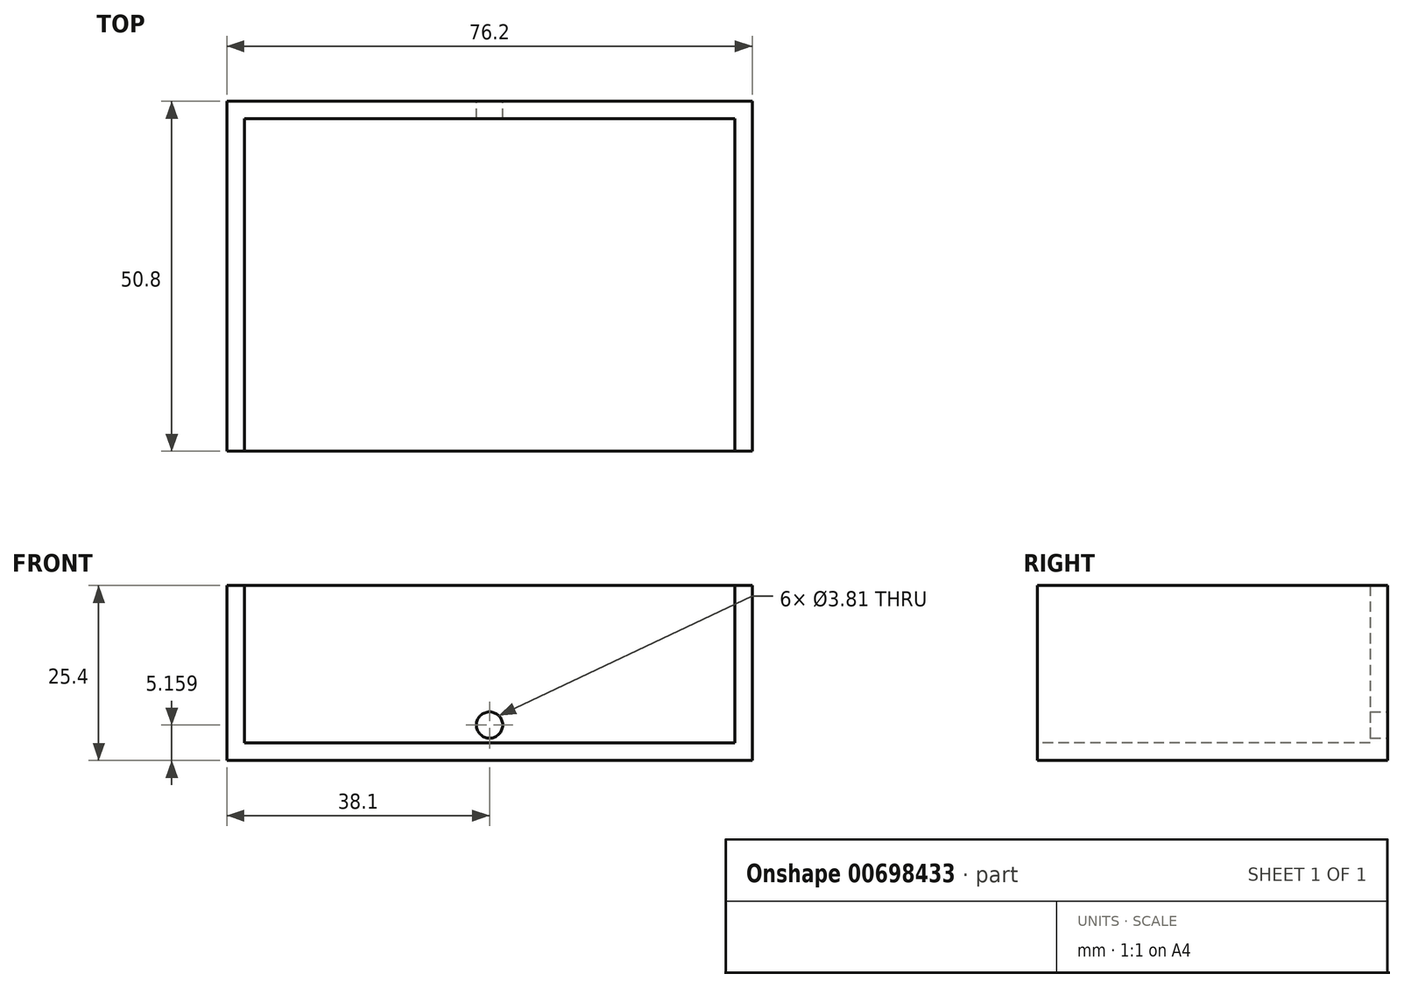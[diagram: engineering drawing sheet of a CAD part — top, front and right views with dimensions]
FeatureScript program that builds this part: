
annotation { "Feature Type Name" : "Feature", "Feature Type Description" : "" }
export const myFeature = defineFeature(function(context is Context, id is Id, definition is map)
    precondition{}
    {
        {
            var Q0;
            Q0=qCreatedBy(makeId("Top.planeOp"),FACE);
            var sketch = newSketch(context, id + "F0", { "sketchPlane" : qUnion([Q0])});
            skLineSegment(sketch, "E0.bottom", {"start": v(-38.1, 25.4) * mm, "end": v(38.1, 25.4) * mm});
            skLineSegment(sketch, "E0.top", {"start": v(-38.1, -25.4) * mm, "end": v(38.1, -25.4) * mm});
            skLineSegment(sketch, "E0.left", {"start": v(-38.1, 25.4) * mm, "end": v(-38.1, -25.4) * mm});
            skLineSegment(sketch, "E0.right", {"start": v(38.1, 25.4) * mm, "end": v(38.1, -25.4) * mm});
            skPoint(sketch, "E0.middle", {"position": v(0, 0) * mm});
            skSolve(sketch);
        }
        {
            var Q0;
            Q0=makeQuery(id+"F0.imprint","IMPRINT",FACE,{"disambiguationData":[TD([[makeQuery(id+"F0.imprint","IMPRINT",EDGE,{"derivedFrom":sQuery(id+"F0.wireOp",EDGE,"E0.bottom")}),-1.0]])]});
            extrude(context, id + "F1", {"entities" : qUnion([Q0]), "depth" : 25.4 * mm, "offsetDistance" : 25.4 * mm});
        }
        {
            var Q0;
            Q0=makeQuery(id+"F1.opExtrude","CAP_FACE",FACE,{"disambiguationData":[OSD([sQuery(id+"F0.wireOp",EDGE,"E0.bottom"),sQuery(id+"F0.wireOp",EDGE,"E0.top"),sQuery(id+"F0.wireOp",EDGE,"E0.left"),sQuery(id+"F0.wireOp",EDGE,"E0.right")])],"isStart":false});
            var Q1;
            Q1=makeQuery(id+"F1.opExtrude","SWEPT_FACE",FACE,{"disambiguationData":[OSD([sQuery(id+"F0.wireOp",EDGE,"E0.top")])]});
            shell(context, id + "F2", {"entities" : qUnion([Q0, Q1]), "thickness" : 2.54 * mm});
        }
        {
            var Q0;
            Q0=makeQuery(id+"F1.opExtrude","SWEPT_FACE",FACE,{"disambiguationData":[OSD([sQuery(id+"F0.wireOp",EDGE,"E0.bottom")])]});
            var sketch = newSketch(context, id + "F3", { "sketchPlane" : qUnion([Q0])});
            skPoint(sketch, "E1", {"position": v(0, 5.16) * mm});
            skSolve(sketch);
        }
        {
            var Q0;
            Q0=sQuery(id+"F3.wireOp",VERTEX,"E1");
            var Q1;
            Q1=makeQuery(id+"F1.opExtrude","SWEPT_BODY",BODY,{"disambiguationData":[OSD([sQuery(id+"F0.wireOp",EDGE,"E0.bottom"),sQuery(id+"F0.wireOp",EDGE,"E0.top"),sQuery(id+"F0.wireOp",EDGE,"E0.left"),sQuery(id+"F0.wireOp",EDGE,"E0.right")])]});
            hole(context, id + "F4", {"style" : HoleStyle.SIMPLE, "endStyle" : HoleEndStyle.THROUGH, "holeDiameter" : 3.8 * mm, "majorDiameter" : 6.35 * mm, "isTappedThrough" : true, "tappedDepth" : 12.7 * mm, "tapClearance" : 3, "locations" : qUnion([Q0]), "scope" : qUnion([Q1])});
        }
    });
